# Revit family: Kubus M LED 1-s Sentr (skrått 45 grader opp mot venstre_veggmontasje)_
name_source: partatom
category: Lighting Fixtures
revit_build: Autodesk Revit 2013 (Build: 20130531_2115(x64)
units: mm (PartAtom-declared; Revit-internal decimal feet)

## types (3) — shared parameters
Apparent Load = 17 VA
Body Material and Colour = Default
Color Filter = 16777215
Dimming Lamp Color Temperature Shift = <None>
Emit Shape Visible in Rendering = No
Lamp = 1
Number of Poles = 1
Photometric Web File = 20x42A12.ies
Tilt Angle = 90.00°
Voltage = 230 V
Wattage Comments = 17 W
Width = 70 mm  [stored 0.229659 ft]

## per-type parameters (varying)
| type | 23m | 35m | 60m | Emit from Rectangle Length | Emit from Rectangle Width | Height | Height 1 | Length | Length 1 |
| 23m | Yes | No | No | 255 mm  [stored 0.836614 ft] | 140 mm  [stored 0.459318 ft] | 140 mm  [stored 0.459318 ft] | 110 mm  [stored 0.360892 ft] | 255 mm  [stored 0.836614 ft] | 225 mm  [stored 0.738189 ft] |
| 35m | No | Yes | No | 376 mm  [stored 1.2336 ft] | 200 mm  [stored 0.656168 ft] | 200 mm  [stored 0.656168 ft] | 170 mm  [stored 0.557743 ft] | 376 mm  [stored 1.2336 ft] | 346 mm  [stored 1.13517 ft] |
| 60m | No | No | Yes | 605 mm  [stored 1.98491 ft] | 315 mm  [stored 1.03346 ft] | 315 mm  [stored 1.03346 ft] | 285 mm | 605 mm  [stored 1.98491 ft] | 575 mm  [stored 1.88648 ft] |

note: [stored X ft] marks values corroborated as IEEE doubles in the binary element streams (Revit-internal decimal feet)

## geometry (parser evidence)
native form markers: Blend x1, Sweep x13
no freeform markers — native parametric forms only
